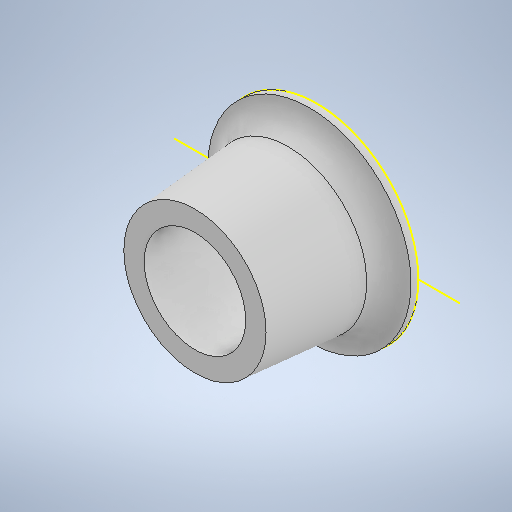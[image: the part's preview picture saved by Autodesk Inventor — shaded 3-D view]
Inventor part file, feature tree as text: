
AUTODESK INVENTOR PART (.ipt)
format: ipt  version: 2025.2 (Build 292293000, 293)  size: 272,384 bytes
history: native  units: mm
features: sketch x2, revolve x1
ambient origin geometry x8: Origin, YZ Plane, XZ Plane, XY Plane, X Axis, Y Axis, Z Axis, Center Point
bodies: Volumenkörper1 (feature_tree)
feature tree (3):
  revolve  "Umdrehung1"
  sketch  "Skizze2"  dims[d3=8.0mm d4=12.0mm d5=90.0deg d6=2.0mm d7=1.0mm d8=2.0mm]
  sketch  "Skizze1"  dims[d2=20.0mm]
